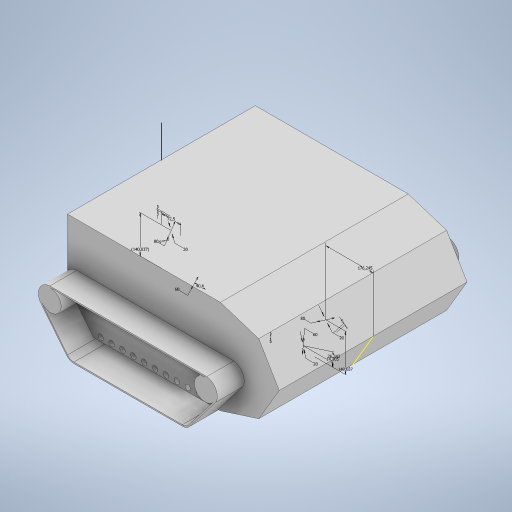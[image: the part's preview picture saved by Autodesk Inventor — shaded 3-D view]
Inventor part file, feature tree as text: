
AUTODESK INVENTOR PART (.ipt)
format: ipt  version: 2023 (Build 270158000, 158)  size: 395,776 bytes
history: native  units: mm
features: extrude x14, sketch x2
ambient origin geometry x8: Origin, YZ Plane, XZ Plane, XY Plane, X Axis, Y Axis, Z Axis, Center Point
bodies: Solido1 (feature_tree)
feature tree (16):
  sketch  "Schizzo1"
  extrude  "Estrusione1"  Depth=600.0mm
  extrude  "Estrusione2"  Depth=350.0mm
  sketch  "Schizzo2"
  extrude  "Estrusione3"  Depth=150.0mm
  extrude  "Estrusione6"  Depth=150.0mm
  extrude  "Estrusione7"  Depth=150.0mm
  extrude  "Estrusione8"  Depth=150.0mm
  extrude  "Estrusione9"  Depth=3.103677mm
  extrude  "Estrusione10"  Depth=10.377397mm
  extrude  "Estrusione11"  Depth=30.0mm
  extrude  "Estrusione12"  Depth=30.0mm
  extrude  "Estrusione13"  Depth=30.0mm
  extrude  "Estrusione14"  Depth=117.867906mm
  extrude  "Estrusione15"  Depth=124.525778mm
  extrude  "Estrusione17"  Depth=700.0mm TaperAngle=0.0deg
